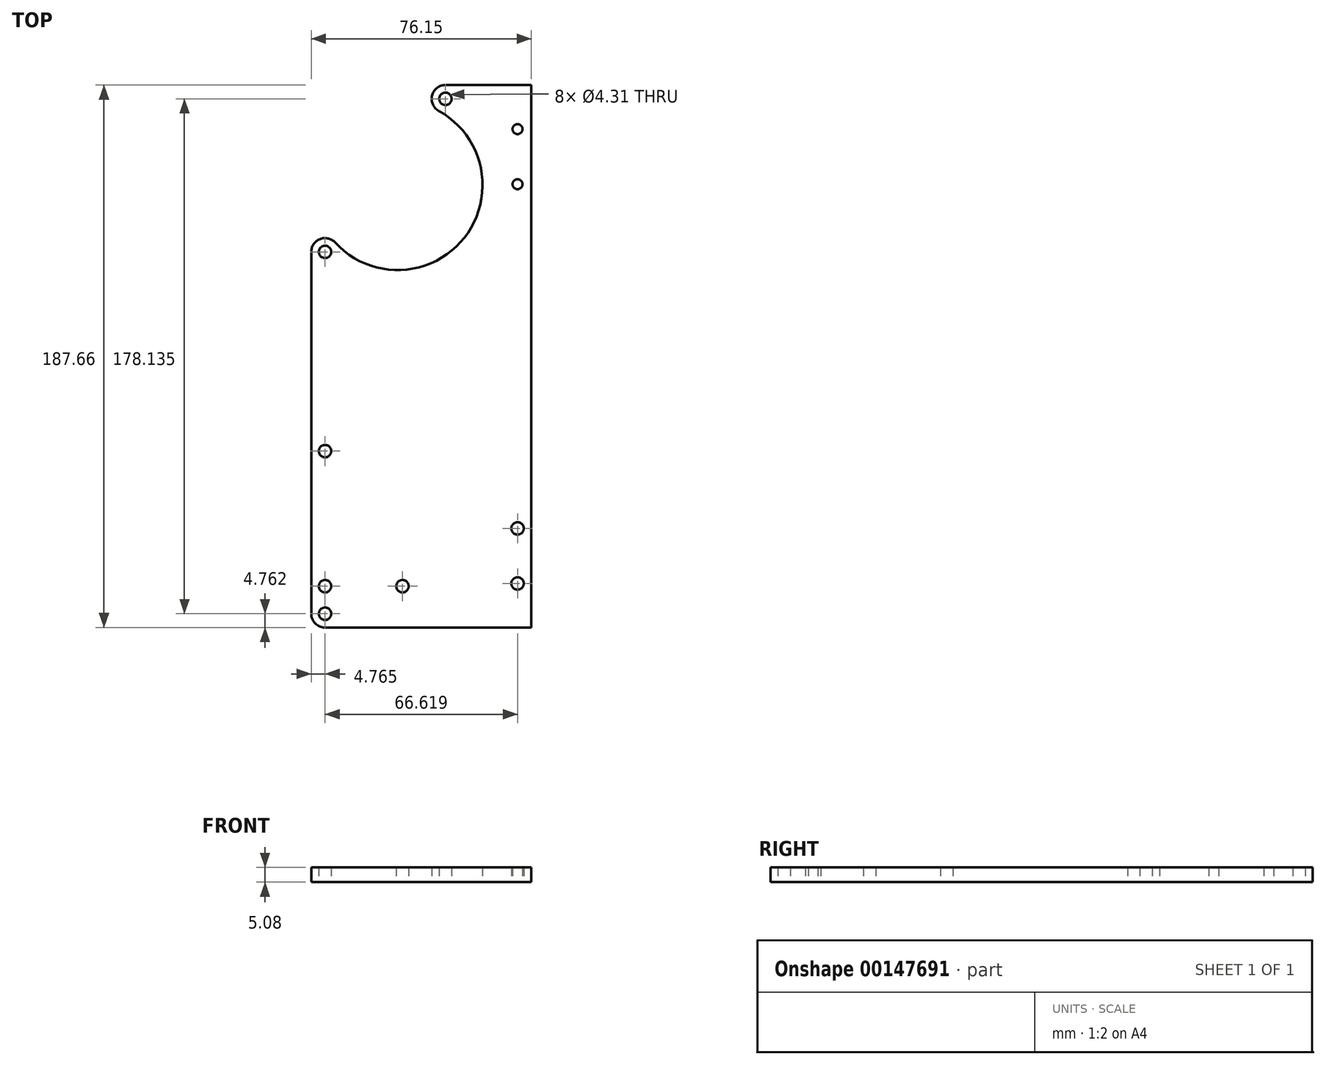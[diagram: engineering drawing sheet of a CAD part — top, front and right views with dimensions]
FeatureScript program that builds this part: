
annotation { "Feature Type Name" : "Feature", "Feature Type Description" : "" }
export const myFeature = defineFeature(function(context is Context, id is Id, definition is map)
    precondition{}
    {
        {
            var Q0;
            Q0=qCreatedBy(makeId("Top.planeOp"),FACE);
            var sketch = newSketch(context, id + "F0", { "sketchPlane" : qUnion([Q0])});
            skLineSegment(sketch, "E0.bottom", {"start": v(46.24, -153.03) * mm, "end": v(-25.14, -153.03) * mm});
            skLineSegment(sketch, "E1", {"start": v(41.47, -153.03) * mm, "end": v(41.47, -137.8) * mm, "construction": true});
            skLineSegment(sketch, "E2", {"start": v(41.47, -137.8) * mm, "end": v(41.47, -118.74) * mm, "construction": true});
            skLineSegment(sketch, "E3", {"start": v(41.47, 34.63) * mm, "end": v(41.47, 19.39) * mm, "construction": true});
            skLineSegment(sketch, "E4", {"start": v(41.47, 19.39) * mm, "end": v(41.47, 0.34) * mm, "construction": true});
            skCircle(sketch, "E5", {"center": v(41.47, 19.39) * mm, "radius": 1.73 * mm});
            skCircle(sketch, "E6", {"center": v(41.47, 0.34) * mm, "radius": 1.73 * mm});
            skCircle(sketch, "E7", {"center": v(41.47, -118.74) * mm, "radius": 2.15 * mm});
            skCircle(sketch, "E8", {"center": v(41.47, -137.8) * mm, "radius": 2.15 * mm});
            skLineSegment(sketch, "E9", {"start": v(1.65, -138.74) * mm, "end": v(-25.14, -138.74) * mm, "construction": true});
            skLineSegment(sketch, "E10", {"start": v(-25.14, -138.74) * mm, "end": v(-25.14, -92.02) * mm, "construction": true});
            skCircle(sketch, "E11", {"center": v(-25.14, -92.02) * mm, "radius": 2.15 * mm});
            skCircle(sketch, "E12", {"center": v(-25.14, -138.74) * mm, "radius": 2.15 * mm});
            skCircle(sketch, "E13", {"center": v(1.65, -138.74) * mm, "radius": 2.15 * mm});
            skArc(sketch, "E14", {"start": v(-29.9, -148.27) * mm, "mid": v(-28.51, -151.64) * mm, "end": v(-25.14, -153.03) * mm});
            skLineSegment(sketch, "E15", {"start": v(46.24, 34.63) * mm, "end": v(46.24, -153.03) * mm});
            skLineSegment(sketch, "E16", {"start": v(-29.9, -148.27) * mm, "end": v(-29.9, -23.08) * mm});
            skLineSegment(sketch, "E17", {"start": v(46.24, 34.63) * mm, "end": v(16.52, 34.63) * mm});
            skArc(sketch, "E18", {"start": v(16.52, 34.63) * mm, "mid": v(11.9, 31.06) * mm, "end": v(14.22, 25.7) * mm});
            skArc(sketch, "E19", {"start": v(-21.64, -19.86) * mm, "mid": v(-26.87, -18.64) * mm, "end": v(-29.9, -23.08) * mm});
            skArc(sketch, "E20", {"start": v(-21.64, -19.86) * mm, "mid": v(23.08, -18.16) * mm, "end": v(14.22, 25.7) * mm});
            skCircle(sketch, "E21", {"center": v(-25.14, -23.08) * mm, "radius": 2.15 * mm});
            skCircle(sketch, "E22", {"center": v(16.52, 29.87) * mm, "radius": 2.15 * mm});
            skLineSegment(sketch, "E23", {"start": v(-25.14, -148.27) * mm, "end": v(-25.14, -138.74) * mm, "construction": true});
            skCircle(sketch, "E24", {"center": v(-25.14, -148.27) * mm, "radius": 2.15 * mm});
            skSolve(sketch);
        }
        {
            var Q0;
            Q0=qSketchRegion(id+"F0",true);
            extrude(context, id + "F1", {"entities" : qUnion([Q0]), "depth" : 5.08 * mm});
        }
    });
